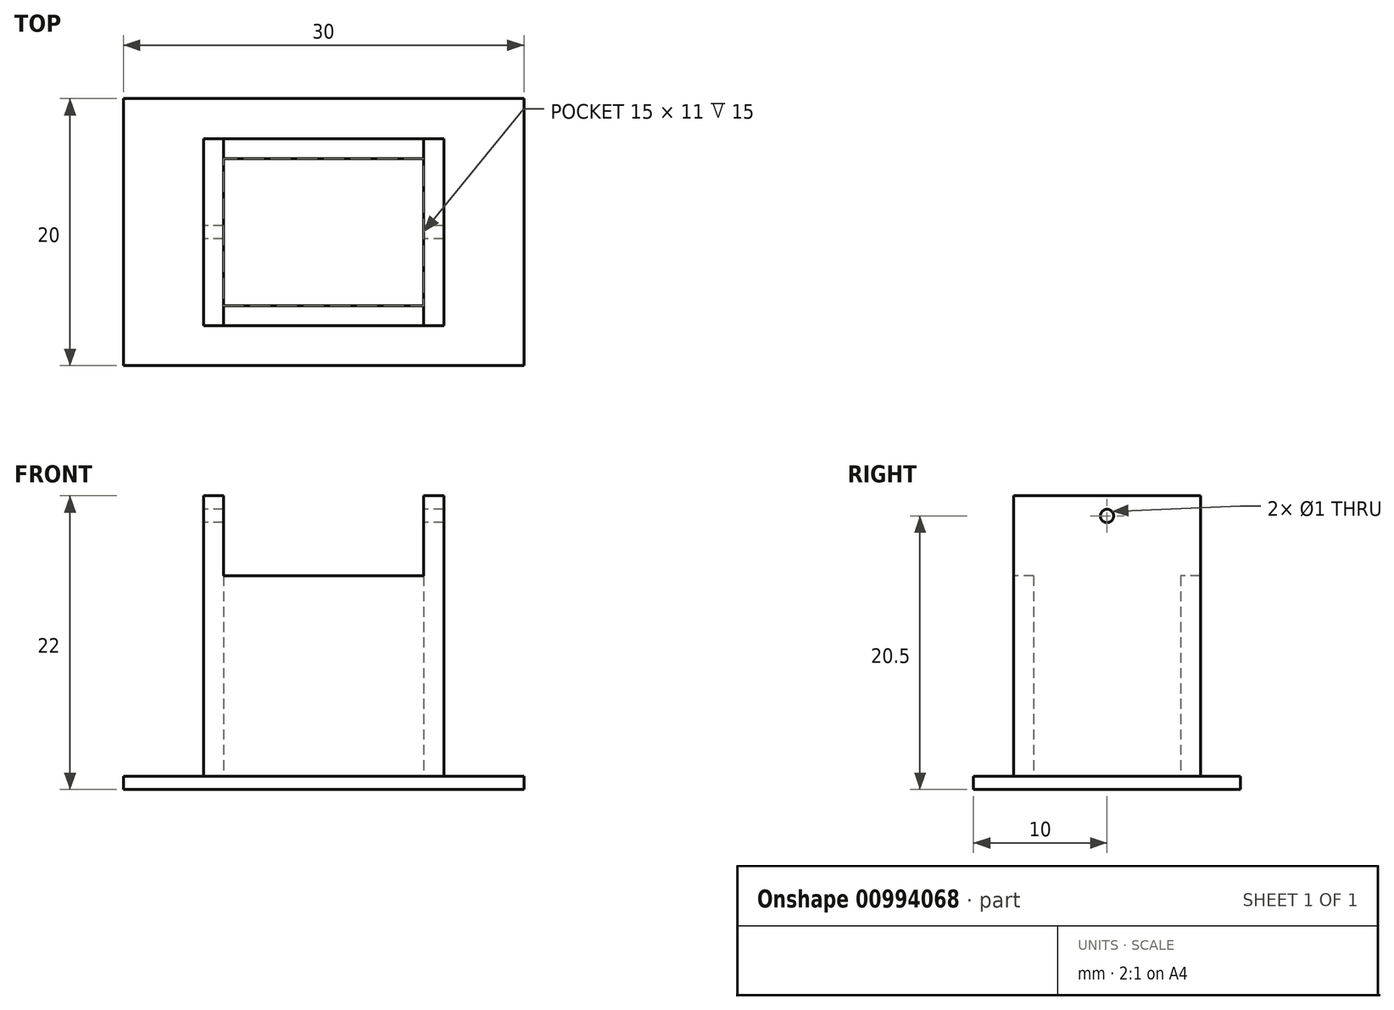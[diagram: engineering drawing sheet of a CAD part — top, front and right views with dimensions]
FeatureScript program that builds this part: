
annotation { "Feature Type Name" : "Feature", "Feature Type Description" : "" }
export const myFeature = defineFeature(function(context is Context, id is Id, definition is map)
    precondition{}
    {
        {
            var Q0;
            Q0=qCreatedBy(makeId("Top.planeOp"),FACE);
            var sketch = newSketch(context, id + "F0", { "sketchPlane" : qUnion([Q0])});
            skLineSegment(sketch, "E0.bottom", {"start": v(0, 0) * mm, "end": v(30, 0) * mm});
            skLineSegment(sketch, "E0.top", {"start": v(0, 20) * mm, "end": v(30, 20) * mm});
            skLineSegment(sketch, "E0.left", {"start": v(0, 0) * mm, "end": v(0, 20) * mm});
            skLineSegment(sketch, "E0.right", {"start": v(30, 0) * mm, "end": v(30, 20) * mm});
            skSolve(sketch);
        }
        {
            var Q0;
            Q0=makeQuery(id+"F0.imprint","IMPRINT",FACE,{"disambiguationData":[TD([[makeQuery(id+"F0.imprint","IMPRINT",EDGE,{"derivedFrom":sQuery(id+"F0.wireOp",EDGE,"E0.bottom")}),1.0]])]});
            extrude(context, id + "F1", {"entities" : qUnion([Q0]), "depth" : 1 * mm, "offsetDistance" : 25 * mm});
        }
        {
            var Q0;
            Q0=makeQuery(id+"F1.opExtrude","CAP_FACE",FACE,{"disambiguationData":[OSD([sQuery(id+"F0.wireOp",EDGE,"E0.bottom"),sQuery(id+"F0.wireOp",EDGE,"E0.top"),sQuery(id+"F0.wireOp",EDGE,"E0.left"),sQuery(id+"F0.wireOp",EDGE,"E0.right")])],"isStart":false});
            var sketch = newSketch(context, id + "F2", { "sketchPlane" : qUnion([Q0])});
            skLineSegment(sketch, "E1.bottom", {"start": v(7.5, 15.5) * mm, "end": v(22.5, 15.5) * mm});
            skLineSegment(sketch, "E1.top", {"start": v(7.5, 4.5) * mm, "end": v(22.5, 4.5) * mm});
            skLineSegment(sketch, "E1.left", {"start": v(7.5, 15.5) * mm, "end": v(7.5, 4.5) * mm});
            skLineSegment(sketch, "E1.right", {"start": v(22.5, 15.5) * mm, "end": v(22.5, 4.5) * mm});
            skLineSegment(sketch, "E2.bottom", {"start": v(6, 17) * mm, "end": v(24, 17) * mm});
            skLineSegment(sketch, "E2.top", {"start": v(6, 3) * mm, "end": v(24, 3) * mm});
            skLineSegment(sketch, "E2.left", {"start": v(6, 17) * mm, "end": v(6, 3) * mm});
            skLineSegment(sketch, "E2.right", {"start": v(24, 17) * mm, "end": v(24, 3) * mm});
            skSolve(sketch);
        }
        {
            var Q0;
            Q0 = qSketchRegion(id + "F2", true);
            extrude(context, id + "F3", {"entities" : qUnion([Q0]), "operationType" : NewBodyOperationType.ADD, "depth" : 15 * mm, "offsetDistance" : 25 * mm});
        }
        {
            var Q0;
            Q0=makeQuery(id+"F3.opExtrude","CAP_FACE",FACE,{"disambiguationData":[OSD([sQuery(id+"F2.wireOp",EDGE,"E1.bottom"),sQuery(id+"F2.wireOp",EDGE,"E1.top"),sQuery(id+"F2.wireOp",EDGE,"E1.left"),sQuery(id+"F2.wireOp",EDGE,"E1.right"),sQuery(id+"F2.wireOp",EDGE,"E2.bottom"),sQuery(id+"F2.wireOp",EDGE,"E2.top"),sQuery(id+"F2.wireOp",EDGE,"E2.left"),sQuery(id+"F2.wireOp",EDGE,"E2.right")])],"isStart":false});
            var sketch = newSketch(context, id + "F4", { "sketchPlane" : qUnion([Q0])});
            skLineSegment(sketch, "E3.bottom", {"start": v(6, 17) * mm, "end": v(7.5, 17) * mm});
            skLineSegment(sketch, "E3.top", {"start": v(6, 3) * mm, "end": v(7.5, 3) * mm});
            skLineSegment(sketch, "E3.left", {"start": v(6, 17) * mm, "end": v(6, 3) * mm});
            skLineSegment(sketch, "E3.right", {"start": v(7.5, 17) * mm, "end": v(7.5, 3) * mm});
            skLineSegment(sketch, "E4.bottom", {"start": v(24, 17) * mm, "end": v(22.5, 17) * mm});
            skLineSegment(sketch, "E4.top", {"start": v(24, 3) * mm, "end": v(22.5, 3) * mm});
            skLineSegment(sketch, "E4.left", {"start": v(24, 17) * mm, "end": v(24, 3) * mm});
            skLineSegment(sketch, "E4.right", {"start": v(22.5, 17) * mm, "end": v(22.5, 3) * mm});
            skSolve(sketch);
        }
        {
            var Q0;
            Q0 = qSketchRegion(id + "F4", true);
            extrude(context, id + "F5", {"entities" : qUnion([Q0]), "operationType" : NewBodyOperationType.ADD, "depth" : 6 * mm, "offsetDistance" : 25 * mm});
        }
        {
            var Q0;
            Q0=makeQuery(id+"F5.boolean.opBoolean","MERGE",FACE,{"derivedFrom":[makeQuery(id+"F3.opExtrude","SWEPT_FACE",FACE,{"disambiguationData":[OSD([sQuery(id+"F2.wireOp",EDGE,"E2.left")])]}),makeQuery(id+"F5.opExtrude","SWEPT_FACE",FACE,{"disambiguationData":[OSD([sQuery(id+"F4.wireOp",EDGE,"E3.left")])]})]});
            var sketch = newSketch(context, id + "F6", { "sketchPlane" : qUnion([Q0])});
            skCircle(sketch, "E5", {"center": v(-10, 20.5) * mm, "radius": 0.5 * mm});
            skSolve(sketch);
        }
        {
            var Q0;
            Q0 = qSketchRegion(id + "F6", true);
            extrude(context, id + "F7", {"entities" : qUnion([Q0]), "operationType" : NewBodyOperationType.REMOVE, "endBound" : BoundingType.THROUGH_ALL, "oppositeDirection" : true, "depth" : 25 * mm, "offsetDistance" : 25 * mm});
        }
    });
